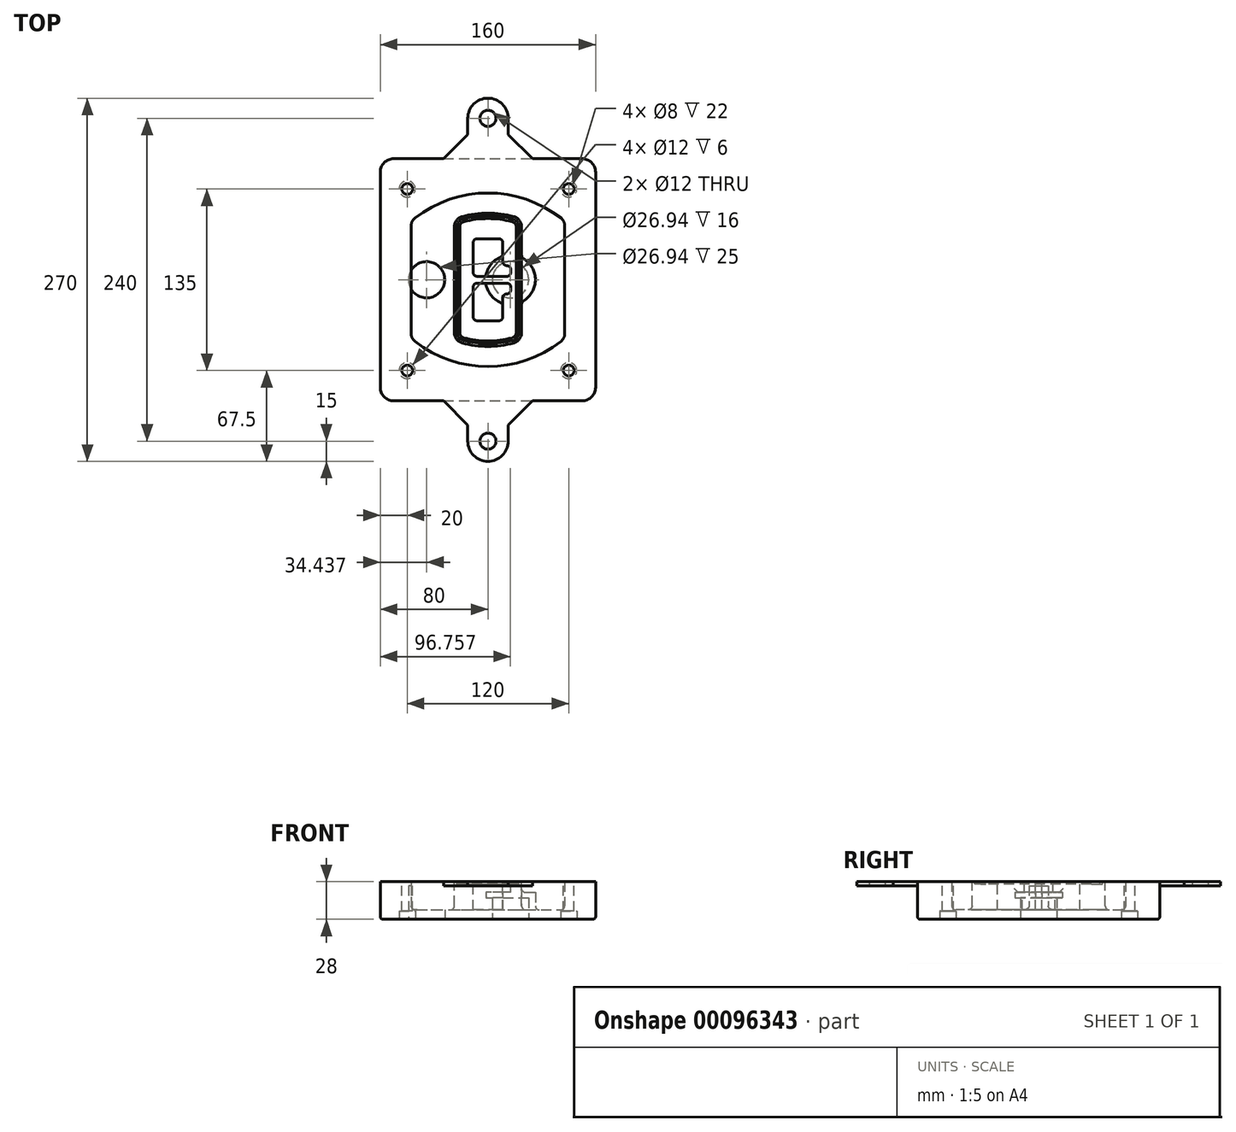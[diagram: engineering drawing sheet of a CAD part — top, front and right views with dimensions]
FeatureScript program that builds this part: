
annotation { "Feature Type Name" : "Feature", "Feature Type Description" : "" }
export const myFeature = defineFeature(function(context is Context, id is Id, definition is map)
    precondition{}
    {
        {
            var Q0;
            Q0=qCreatedBy(makeId("Top.planeOp"),FACE);
            var sketch = newSketch(context, id + "F0", { "sketchPlane" : qUnion([Q0])});
            skPoint(sketch, "E0.rect.middle", {"position": v(0, 0) * mm});
            skLineSegment(sketch, "E1.bottom", {"start": v(-70, -90) * mm, "end": v(70, -90) * mm});
            skLineSegment(sketch, "E1.top", {"start": v(-70, 90) * mm, "end": v(70, 90) * mm});
            skLineSegment(sketch, "E1.left", {"start": v(-80, -80) * mm, "end": v(-80, 80) * mm});
            skLineSegment(sketch, "E1.right", {"start": v(80, -80) * mm, "end": v(80, 80) * mm});
            skLineSegment(sketch, "E2", {"start": v(-80, 90) * mm, "end": v(80, -90) * mm, "construction": true});
            skLineSegment(sketch, "E3", {"start": v(80, 90) * mm, "end": v(-80, -90) * mm, "construction": true});
            skCircle(sketch, "E4", {"center": v(-60, 67.5) * mm, "radius": 4 * mm});
            skCircle(sketch, "E5", {"center": v(60, 67.5) * mm, "radius": 4 * mm});
            skCircle(sketch, "E6", {"center": v(60, -67.5) * mm, "radius": 4 * mm});
            skCircle(sketch, "E7", {"center": v(-60, -67.5) * mm, "radius": 4 * mm});
            skLineSegment(sketch, "E8", {"start": v(-60, 67.5) * mm, "end": v(60, 67.5) * mm, "construction": true});
            skLineSegment(sketch, "E9", {"start": v(60, 67.5) * mm, "end": v(60, -67.5) * mm, "construction": true});
            skLineSegment(sketch, "E10", {"start": v(60, -67.5) * mm, "end": v(-60, -67.5) * mm, "construction": true});
            skLineSegment(sketch, "E11", {"start": v(-60, -67.5) * mm, "end": v(-60, 67.5) * mm, "construction": true});
            skLineSegment(sketch, "E12", {"start": v(-60, 40.3) * mm, "end": v(-60, -40.3) * mm});
            skLineSegment(sketch, "E13", {"start": v(60, 40.3) * mm, "end": v(60, -40.3) * mm});
            skArc(sketch, "E14", {"start": v(56.15, 48.18) * mm, "mid": v(0, 67.5) * mm, "end": v(-56.15, 48.18) * mm});
            skArc(sketch, "E15", {"start": v(-56.15, -48.18) * mm, "mid": v(0, -67.5) * mm, "end": v(56.15, -48.18) * mm});
            skLineSegment(sketch, "E16", {"start": v(-60, 0) * mm, "end": v(60, 0) * mm, "construction": true});
            skPoint(sketch, "E17.visualSharp", {"position": v(-60, -45) * mm});
            skArc(sketch, "E17.filletArc", {"start": v(-60, -40.3) * mm, "mid": v(-58.99, -44.68) * mm, "end": v(-56.15, -48.18) * mm});
            skPoint(sketch, "E18.visualSharp", {"position": v(-60, 45) * mm});
            skArc(sketch, "E18.filletArc", {"start": v(-56.15, 48.18) * mm, "mid": v(-58.99, 44.68) * mm, "end": v(-60, 40.3) * mm});
            skPoint(sketch, "E19.visualSharp", {"position": v(60, 45) * mm});
            skArc(sketch, "E19.filletArc", {"start": v(60, 40.3) * mm, "mid": v(58.99, 44.68) * mm, "end": v(56.15, 48.18) * mm});
            skPoint(sketch, "E20.visualSharp", {"position": v(60, -45) * mm});
            skArc(sketch, "E20.filletArc", {"start": v(56.15, -48.18) * mm, "mid": v(58.99, -44.68) * mm, "end": v(60, -40.3) * mm});
            skPoint(sketch, "E21.visualSharp", {"position": v(-80, 90) * mm});
            skArc(sketch, "E21.filletArc", {"start": v(-70, 90) * mm, "mid": v(-77.07, 87.07) * mm, "end": v(-80, 80) * mm});
            skPoint(sketch, "E22.visualSharp", {"position": v(80, 90) * mm});
            skArc(sketch, "E22.filletArc", {"start": v(80, 80) * mm, "mid": v(77.07, 87.07) * mm, "end": v(70, 90) * mm});
            skPoint(sketch, "E23.visualSharp", {"position": v(80, -90) * mm});
            skArc(sketch, "E23.filletArc", {"start": v(70, -90) * mm, "mid": v(77.07, -87.07) * mm, "end": v(80, -80) * mm});
            skPoint(sketch, "E24.visualSharp", {"position": v(-80, -90) * mm});
            skArc(sketch, "E24.filletArc", {"start": v(-80, -80) * mm, "mid": v(-77.07, -87.07) * mm, "end": v(-70, -90) * mm});
            skArc(sketch, "E25.0", {"start": v(57, 40.3) * mm, "mid": v(56.3, 43.36) * mm, "end": v(54.3, 45.81) * mm});
            skLineSegment(sketch, "E25.1", {"start": v(57, 40.3) * mm, "end": v(57, -40.3) * mm});
            skArc(sketch, "E25.2", {"start": v(54.3, -45.81) * mm, "mid": v(56.3, -43.36) * mm, "end": v(57, -40.3) * mm});
            skArc(sketch, "E25.3", {"start": v(-54.3, -45.81) * mm, "mid": v(0, -64.5) * mm, "end": v(54.3, -45.81) * mm});
            skArc(sketch, "E25.4", {"start": v(-57, -40.3) * mm, "mid": v(-56.3, -43.36) * mm, "end": v(-54.3, -45.81) * mm});
            skArc(sketch, "E25.5", {"start": v(54.3, 45.81) * mm, "mid": v(0, 64.5) * mm, "end": v(-54.3, 45.81) * mm});
            skLineSegment(sketch, "E25.6", {"start": v(-57, 40.3) * mm, "end": v(-57, -40.3) * mm});
            skArc(sketch, "E25.7", {"start": v(-54.3, 45.81) * mm, "mid": v(-56.3, 43.36) * mm, "end": v(-57, 40.3) * mm});
            skArc(sketch, "E26.0", {"start": v(-58.62, 51.33) * mm, "mid": v(-62.58, 46.43) * mm, "end": v(-64, 40.3) * mm});
            skArc(sketch, "E26.1", {"start": v(58.62, 51.33) * mm, "mid": v(0, 71.5) * mm, "end": v(-58.62, 51.33) * mm});
            skArc(sketch, "E26.2", {"start": v(64, 40.3) * mm, "mid": v(62.58, 46.43) * mm, "end": v(58.62, 51.33) * mm});
            skLineSegment(sketch, "E26.3", {"start": v(64, 40.3) * mm, "end": v(64, -40.3) * mm});
            skArc(sketch, "E26.4", {"start": v(58.62, -51.33) * mm, "mid": v(62.58, -46.43) * mm, "end": v(64, -40.3) * mm});
            skLineSegment(sketch, "E26.5", {"start": v(-64, 40.3) * mm, "end": v(-64, -40.3) * mm});
            skArc(sketch, "E26.6", {"start": v(-58.62, -51.33) * mm, "mid": v(0, -71.5) * mm, "end": v(58.62, -51.33) * mm});
            skArc(sketch, "E26.7", {"start": v(-64, -40.3) * mm, "mid": v(-62.58, -46.43) * mm, "end": v(-58.62, -51.33) * mm});
            skSolve(sketch);
        }
        {
            var Q0;
            Q0=makeQuery(id+"F0.imprint","IMPRINT",FACE,{"disambiguationData":[TD([[makeQuery(id+"F0.imprint","IMPRINT",EDGE,{"derivedFrom":sQuery(id+"F0.wireOp",EDGE,"E1.bottom")}),1.0]])]});
            var Q1;
            Q1=makeQuery(id+"F0.imprint","IMPRINT",FACE,{"disambiguationData":[TD([[makeQuery(id+"F0.imprint","IMPRINT",EDGE,{"derivedFrom":sQuery(id+"F0.wireOp",EDGE,"E12")}),1.0]])]});
            var Q2;
            Q2=makeQuery(id+"F0.imprint","IMPRINT",FACE,{"disambiguationData":[TD([[makeQuery(id+"F0.imprint","IMPRINT",EDGE,{"derivedFrom":sQuery(id+"F0.wireOp",EDGE,"E25.0")}),1.0]])]});
            var Q3;
            Q3=makeQuery(id+"F0.imprint","IMPRINT",FACE,{"disambiguationData":[TD([[makeQuery(id+"F0.imprint","IMPRINT",EDGE,{"derivedFrom":sQuery(id+"F0.wireOp",EDGE,"E12")}),-1.0]])]});
            extrude(context, id + "F1", {"entities" : qUnion([Q0, Q1, Q2, Q3]), "oppositeDirection" : true, "depth" : 25 * mm});
        }
        {
            var Q0;
            Q0=makeQuery(id+"F0.imprint","IMPRINT",FACE,{"disambiguationData":[TD([[makeQuery(id+"F0.imprint","IMPRINT",EDGE,{"derivedFrom":sQuery(id+"F0.wireOp",EDGE,"E12")}),1.0]])]});
            extrude(context, id + "F2", {"entities" : qUnion([Q0]), "operationType" : NewBodyOperationType.ADD, "depth" : 3 * mm});
        }
        {
            var Q0;
            Q0=makeQuery(id+"F0.imprint","IMPRINT",FACE,{"disambiguationData":[TD([[makeQuery(id+"F0.imprint","IMPRINT",EDGE,{"derivedFrom":sQuery(id+"F0.wireOp",EDGE,"E25.0")}),1.0]])]});
            extrude(context, id + "F3", {"entities" : qUnion([Q0]), "operationType" : NewBodyOperationType.REMOVE, "oppositeDirection" : true, "depth" : 18 * mm});
        }
        {
            var Q0;
            Q0=makeQuery(id+"F2.opExtrude","CAP_FACE",FACE,{"disambiguationData":[OSD([sQuery(id+"F0.wireOp",EDGE,"E12"),sQuery(id+"F0.wireOp",EDGE,"E13"),sQuery(id+"F0.wireOp",EDGE,"E14"),sQuery(id+"F0.wireOp",EDGE,"E15"),sQuery(id+"F0.wireOp",EDGE,"E17.filletArc"),sQuery(id+"F0.wireOp",EDGE,"E18.filletArc"),sQuery(id+"F0.wireOp",EDGE,"E19.filletArc"),sQuery(id+"F0.wireOp",EDGE,"E20.filletArc"),sQuery(id+"F0.wireOp",EDGE,"E25.0"),sQuery(id+"F0.wireOp",EDGE,"E25.1"),sQuery(id+"F0.wireOp",EDGE,"E25.2"),sQuery(id+"F0.wireOp",EDGE,"E25.3"),sQuery(id+"F0.wireOp",EDGE,"E25.4"),sQuery(id+"F0.wireOp",EDGE,"E25.5"),sQuery(id+"F0.wireOp",EDGE,"E25.6"),sQuery(id+"F0.wireOp",EDGE,"E25.7")])],"isStart":false});
            var sketch = newSketch(context, id + "F4", { "sketchPlane" : qUnion([Q0])});
            skArc(sketch, "E27.0", {"start": v(-19.08, -46.97) * mm, "mid": v(0, -49.5) * mm, "end": v(19.08, -46.97) * mm});
            skArc(sketch, "E28.0", {"start": v(19.08, 46.97) * mm, "mid": v(0, 49.5) * mm, "end": v(-19.08, 46.97) * mm});
            skLineSegment(sketch, "E29", {"start": v(-25, 39.25) * mm, "end": v(-25, -39.25) * mm});
            skLineSegment(sketch, "E30", {"start": v(25, 39.25) * mm, "end": v(25, -39.25) * mm});
            skLineSegment(sketch, "E31", {"start": v(-25, 45.1) * mm, "end": v(25, 45.1) * mm, "construction": true});
            skLineSegment(sketch, "E32", {"start": v(-25, -45.1) * mm, "end": v(25, -45.1) * mm, "construction": true});
            skPoint(sketch, "E33.visualSharp", {"position": v(-25, 45.1) * mm});
            skArc(sketch, "E33.filletArc", {"start": v(-19.08, 46.97) * mm, "mid": v(-23.35, 44.11) * mm, "end": v(-25, 39.25) * mm});
            skPoint(sketch, "E34.visualSharp", {"position": v(25, 45.1) * mm});
            skArc(sketch, "E34.filletArc", {"start": v(25, 39.25) * mm, "mid": v(23.35, 44.11) * mm, "end": v(19.08, 46.97) * mm});
            skPoint(sketch, "E35.visualSharp", {"position": v(25, -45.1) * mm});
            skArc(sketch, "E35.filletArc", {"start": v(19.08, -46.97) * mm, "mid": v(23.35, -44.11) * mm, "end": v(25, -39.25) * mm});
            skPoint(sketch, "E36.visualSharp", {"position": v(-25, -45.1) * mm});
            skArc(sketch, "E36.filletArc", {"start": v(-25, -39.25) * mm, "mid": v(-23.35, -44.11) * mm, "end": v(-19.08, -46.97) * mm});
            skArc(sketch, "E37.0", {"start": v(54.3, 45.81) * mm, "mid": v(0, 64.5) * mm, "end": v(-54.3, 45.81) * mm});
            skArc(sketch, "E37.1", {"start": v(-54.3, 45.81) * mm, "mid": v(-56.3, 43.36) * mm, "end": v(-57, 40.3) * mm});
            skLineSegment(sketch, "E37.2", {"start": v(-57, 40.3) * mm, "end": v(-57, -40.3) * mm});
            skArc(sketch, "E37.3", {"start": v(-57, -40.3) * mm, "mid": v(-56.3, -43.36) * mm, "end": v(-54.3, -45.81) * mm});
            skArc(sketch, "E37.4", {"start": v(-54.3, -45.81) * mm, "mid": v(0, -64.5) * mm, "end": v(54.3, -45.81) * mm});
            skArc(sketch, "E37.5", {"start": v(54.3, -45.81) * mm, "mid": v(56.3, -43.36) * mm, "end": v(57, -40.3) * mm});
            skLineSegment(sketch, "E37.6", {"start": v(57, 40.3) * mm, "end": v(57, -40.3) * mm});
            skArc(sketch, "E37.7", {"start": v(57, 40.3) * mm, "mid": v(56.3, 43.36) * mm, "end": v(54.3, 45.81) * mm});
            skLineSegment(sketch, "E38.0", {"start": v(23, 39.25) * mm, "end": v(23, -39.25) * mm});
            skArc(sketch, "E38.1", {"start": v(18.56, -45.04) * mm, "mid": v(21.76, -42.9) * mm, "end": v(23, -39.25) * mm});
            skArc(sketch, "E38.2", {"start": v(-18.56, -45.04) * mm, "mid": v(0, -47.5) * mm, "end": v(18.56, -45.04) * mm});
            skArc(sketch, "E38.3", {"start": v(-23, -39.25) * mm, "mid": v(-21.76, -42.9) * mm, "end": v(-18.56, -45.04) * mm});
            skLineSegment(sketch, "E38.4", {"start": v(-23, 39.25) * mm, "end": v(-23, -39.25) * mm});
            skArc(sketch, "E38.5", {"start": v(23, 39.25) * mm, "mid": v(21.76, 42.9) * mm, "end": v(18.56, 45.04) * mm});
            skArc(sketch, "E38.6", {"start": v(-18.56, 45.04) * mm, "mid": v(-21.76, 42.9) * mm, "end": v(-23, 39.25) * mm});
            skArc(sketch, "E38.7", {"start": v(18.56, 45.04) * mm, "mid": v(0, 47.5) * mm, "end": v(-18.56, 45.04) * mm});
            skArc(sketch, "E39.0", {"start": v(21, 39.25) * mm, "mid": v(20.18, 41.68) * mm, "end": v(18.04, 43.1) * mm});
            skLineSegment(sketch, "E39.1", {"start": v(21, 39.25) * mm, "end": v(21, -39.25) * mm});
            skArc(sketch, "E39.2", {"start": v(18.04, -43.1) * mm, "mid": v(20.18, -41.68) * mm, "end": v(21, -39.25) * mm});
            skArc(sketch, "E39.3", {"start": v(-18.04, -43.1) * mm, "mid": v(0, -45.5) * mm, "end": v(18.04, -43.1) * mm});
            skArc(sketch, "E39.4", {"start": v(-21, -39.25) * mm, "mid": v(-20.18, -41.68) * mm, "end": v(-18.04, -43.1) * mm});
            skArc(sketch, "E39.5", {"start": v(18.04, 43.1) * mm, "mid": v(0, 45.5) * mm, "end": v(-18.04, 43.1) * mm});
            skLineSegment(sketch, "E39.6", {"start": v(-21, 39.25) * mm, "end": v(-21, -39.25) * mm});
            skArc(sketch, "E39.7", {"start": v(-18.04, 43.1) * mm, "mid": v(-20.18, 41.68) * mm, "end": v(-21, 39.25) * mm});
            skLineSegment(sketch, "E40", {"start": v(-25, 0) * mm, "end": v(25, 0) * mm, "construction": true});
            skLineSegment(sketch, "E41", {"start": v(-11, 5.5) * mm, "end": v(-11, 27.5) * mm});
            skLineSegment(sketch, "E42", {"start": v(-8, 30.5) * mm, "end": v(8, 30.5) * mm});
            skLineSegment(sketch, "E43", {"start": v(11, 27.5) * mm, "end": v(11, 13.5) * mm});
            skLineSegment(sketch, "E44", {"start": v(14, 10.5) * mm, "end": v(14, 10.5) * mm});
            skLineSegment(sketch, "E45", {"start": v(17, 7.5) * mm, "end": v(17, 5.5) * mm});
            skLineSegment(sketch, "E46", {"start": v(14, 2.5) * mm, "end": v(-8, 2.5) * mm});
            skPoint(sketch, "E47.visualSharp", {"position": v(-11, 30.5) * mm});
            skArc(sketch, "E47.filletArc", {"start": v(-8, 30.5) * mm, "mid": v(-10.12, 29.62) * mm, "end": v(-11, 27.5) * mm});
            skPoint(sketch, "E48.visualSharp", {"position": v(11, 30.5) * mm});
            skArc(sketch, "E48.filletArc", {"start": v(11, 27.5) * mm, "mid": v(10.12, 29.62) * mm, "end": v(8, 30.5) * mm});
            skPoint(sketch, "E49.visualSharp", {"position": v(11, 10.5) * mm});
            skArc(sketch, "E49.filletArc", {"start": v(11, 13.5) * mm, "mid": v(11.88, 11.38) * mm, "end": v(14, 10.5) * mm});
            skPoint(sketch, "E50.visualSharp", {"position": v(17, 10.5) * mm});
            skArc(sketch, "E50.filletArc", {"start": v(17, 7.5) * mm, "mid": v(16.12, 9.62) * mm, "end": v(14, 10.5) * mm});
            skPoint(sketch, "E51.visualSharp", {"position": v(17, 2.5) * mm});
            skArc(sketch, "E51.filletArc", {"start": v(14, 2.5) * mm, "mid": v(16.12, 3.38) * mm, "end": v(17, 5.5) * mm});
            skPoint(sketch, "E52.visualSharp", {"position": v(-11, 2.5) * mm});
            skArc(sketch, "E52.filletArc", {"start": v(-11, 5.5) * mm, "mid": v(-10.12, 3.38) * mm, "end": v(-8, 2.5) * mm});
            skLineSegment(sketch, "E53.0.MirrorCS", {"start": v(14, -2.5) * mm, "end": v(-8, -2.5) * mm});
            skArc(sketch, "E54.0.MirrorCS", {"start": v(-11, -5.5) * mm, "mid": v(-10.12, -3.38) * mm, "end": v(-8, -2.5) * mm});
            skLineSegment(sketch, "E55.0.MirrorCS", {"start": v(-11, -5.5) * mm, "end": v(-11, -27.5) * mm});
            skArc(sketch, "E56.0.MirrorCS", {"start": v(-8, -30.5) * mm, "mid": v(-10.12, -29.62) * mm, "end": v(-11, -27.5) * mm});
            skLineSegment(sketch, "E57.0.MirrorCS", {"start": v(-8, -30.5) * mm, "end": v(8, -30.5) * mm});
            skArc(sketch, "E58.0.MirrorCS", {"start": v(11, -27.5) * mm, "mid": v(10.12, -29.62) * mm, "end": v(8, -30.5) * mm});
            skLineSegment(sketch, "E59.0.MirrorCS", {"start": v(11, -27.5) * mm, "end": v(11, -13.5) * mm});
            skArc(sketch, "E60.0.MirrorCS", {"start": v(11, -13.5) * mm, "mid": v(11.88, -11.38) * mm, "end": v(14, -10.5) * mm});
            skArc(sketch, "E61.0.MirrorCS", {"start": v(17, -7.5) * mm, "mid": v(16.12, -9.62) * mm, "end": v(14, -10.5) * mm});
            skLineSegment(sketch, "E62.0.MirrorCS", {"start": v(17, -7.5) * mm, "end": v(17, -5.5) * mm});
            skArc(sketch, "E63.0.MirrorCS", {"start": v(14, -2.5) * mm, "mid": v(16.12, -3.38) * mm, "end": v(17, -5.5) * mm});
            skSolve(sketch);
        }
        {
            var Q0;
            Q0=makeQuery(id+"F4.imprint","IMPRINT",FACE,{"disambiguationData":[TD([[makeQuery(id+"F4.imprint","IMPRINT",EDGE,{"derivedFrom":sQuery(id+"F4.wireOp",EDGE,"E27.0")}),1.0]])]});
            var Q1;
            Q1=makeQuery(id+"F4.imprint","IMPRINT",FACE,{"disambiguationData":[TD([[makeQuery(id+"F4.imprint","IMPRINT",EDGE,{"derivedFrom":sQuery(id+"F4.wireOp",EDGE,"E38.0")}),-1.0]])]});
            var Q2;
            Q2=makeQuery(id+"F4.imprint","IMPRINT",FACE,{"disambiguationData":[TD([[makeQuery(id+"F4.imprint","IMPRINT",EDGE,{"derivedFrom":sQuery(id+"F4.wireOp",EDGE,"E39.0")}),1.0]])]});
            extrude(context, id + "F5", {"entities" : qUnion([Q0, Q1, Q2]), "operationType" : NewBodyOperationType.ADD, "endBound" : BoundingType.UP_TO_NEXT, "oppositeDirection" : true, "depth" : 25 * mm});
        }
        {
            var Q0;
            Q0=makeQuery(id+"F4.imprint","IMPRINT",FACE,{"disambiguationData":[TD([[makeQuery(id+"F4.imprint","IMPRINT",EDGE,{"derivedFrom":sQuery(id+"F4.wireOp",EDGE,"E38.0")}),-1.0]])]});
            extrude(context, id + "F6", {"entities" : qUnion([Q0]), "operationType" : NewBodyOperationType.REMOVE, "oppositeDirection" : true, "depth" : 2 * mm});
        }
        {
            var Q0;
            Q0=makeQuery(id+"F1.opExtrude","CAP_FACE",FACE,{"disambiguationData":[OSD([sQuery(id+"F0.wireOp",EDGE,"E1.bottom"),sQuery(id+"F0.wireOp",EDGE,"E1.top"),sQuery(id+"F0.wireOp",EDGE,"E1.left"),sQuery(id+"F0.wireOp",EDGE,"E1.right"),sQuery(id+"F0.wireOp",EDGE,"E4"),sQuery(id+"F0.wireOp",EDGE,"E5"),sQuery(id+"F0.wireOp",EDGE,"E6"),sQuery(id+"F0.wireOp",EDGE,"E7"),sQuery(id+"F0.wireOp",EDGE,"E21.filletArc"),sQuery(id+"F0.wireOp",EDGE,"E22.filletArc"),sQuery(id+"F0.wireOp",EDGE,"E23.filletArc"),sQuery(id+"F0.wireOp",EDGE,"E24.filletArc")])],"isStart":false});
            var sketch = newSketch(context, id + "F7", { "sketchPlane" : qUnion([Q0])});
            skCircle(sketch, "E64", {"center": v(16.76, 0) * mm, "radius": 13.47 * mm});
            skCircle(sketch, "E65", {"center": v(-45.56, 0) * mm, "radius": 13.47 * mm});
            skLineSegment(sketch, "E66", {"start": v(80, 0) * mm, "end": v(-80, 0) * mm});
            skCircle(sketch, "E67", {"center": v(16.76, 0) * mm, "radius": 18.47 * mm});
            skCircle(sketch, "E68", {"center": v(60, -67.5) * mm, "radius": 6 * mm});
            skCircle(sketch, "E69", {"center": v(-60, -67.5) * mm, "radius": 6 * mm});
            skCircle(sketch, "E70", {"center": v(-60, 67.5) * mm, "radius": 6 * mm});
            skCircle(sketch, "E71", {"center": v(60, 67.5) * mm, "radius": 6 * mm});
            skSolve(sketch);
        }
        {
            var Q0;
            {var subQ1=sQuery(id+"F7.wireOp",EDGE,"E66");var subQ4=sQuery(id+"F7.wireOp",EDGE,"E64");var subQ6=makeQuery(id+"F7.imprint","INTERSECT",VERTEX,{"disambiguationData":[OD(0.0)],"derivedFrom":[subQ4,subQ1]});Q0=makeQuery(id+"F7.imprint","IMPRINT",FACE,{"disambiguationData":[TD([[makeQuery(id+"F7.imprint","IMPRINT",EDGE,{"disambiguationData":[TD([[subQ6,-1.0]])],"derivedFrom":subQ4}),-1.0]])]});}
            var Q1;
            {var subQ0=sQuery(id+"F7.wireOp",EDGE,"E66");var subQ1=sQuery(id+"F7.wireOp",EDGE,"E64");var subQ3=makeQuery(id+"F7.imprint","INTERSECT",VERTEX,{"disambiguationData":[OD(0.0)],"derivedFrom":[subQ1,subQ0]});Q1=makeQuery(id+"F7.imprint","IMPRINT",FACE,{"disambiguationData":[TD([[makeQuery(id+"F7.imprint","IMPRINT",EDGE,{"disambiguationData":[TD([[subQ3,-1.0]])],"derivedFrom":subQ1}),1.0]])]});}
            var Q2;
            {var subQ0=sQuery(id+"F7.wireOp",EDGE,"E66");var subQ1=sQuery(id+"F7.wireOp",EDGE,"E64");var subQ3=makeQuery(id+"F7.imprint","INTERSECT",VERTEX,{"disambiguationData":[OD(0.0)],"derivedFrom":[subQ1,subQ0]});Q2=makeQuery(id+"F7.imprint","IMPRINT",FACE,{"disambiguationData":[TD([[makeQuery(id+"F7.imprint","IMPRINT",EDGE,{"disambiguationData":[TD([[subQ3,1.0]])],"derivedFrom":subQ1}),1.0]])]});}
            var Q3;
            {var subQ1=sQuery(id+"F7.wireOp",EDGE,"E66");var subQ4=sQuery(id+"F7.wireOp",EDGE,"E64");var subQ6=makeQuery(id+"F7.imprint","INTERSECT",VERTEX,{"disambiguationData":[OD(0.0)],"derivedFrom":[subQ4,subQ1]});Q3=makeQuery(id+"F7.imprint","IMPRINT",FACE,{"disambiguationData":[TD([[makeQuery(id+"F7.imprint","IMPRINT",EDGE,{"disambiguationData":[TD([[subQ6,1.0]])],"derivedFrom":subQ4}),-1.0]])]});}
            extrude(context, id + "F8", {"entities" : qUnion([Q0, Q1, Q2, Q3]), "operationType" : NewBodyOperationType.ADD, "oppositeDirection" : true, "depth" : 20 * mm});
        }
        {
            var Q0;
            {var subQ0=sQuery(id+"F7.wireOp",EDGE,"E66");var subQ1=sQuery(id+"F7.wireOp",EDGE,"E64");var subQ3=makeQuery(id+"F7.imprint","INTERSECT",VERTEX,{"disambiguationData":[OD(0.0)],"derivedFrom":[subQ1,subQ0]});Q0=makeQuery(id+"F7.imprint","IMPRINT",FACE,{"disambiguationData":[TD([[makeQuery(id+"F7.imprint","IMPRINT",EDGE,{"disambiguationData":[TD([[subQ3,-1.0]])],"derivedFrom":subQ1}),1.0]])]});}
            var Q1;
            {var subQ0=sQuery(id+"F7.wireOp",EDGE,"E66");var subQ1=sQuery(id+"F7.wireOp",EDGE,"E64");var subQ3=makeQuery(id+"F7.imprint","INTERSECT",VERTEX,{"disambiguationData":[OD(0.0)],"derivedFrom":[subQ1,subQ0]});Q1=makeQuery(id+"F7.imprint","IMPRINT",FACE,{"disambiguationData":[TD([[makeQuery(id+"F7.imprint","IMPRINT",EDGE,{"disambiguationData":[TD([[subQ3,1.0]])],"derivedFrom":subQ1}),1.0]])]});}
            extrude(context, id + "F9", {"entities" : qUnion([Q0, Q1]), "operationType" : NewBodyOperationType.REMOVE, "oppositeDirection" : true, "depth" : 16 * mm});
        }
        {
            var Q0;
            {var subQ0=sQuery(id+"F7.wireOp",EDGE,"E66");var subQ1=sQuery(id+"F7.wireOp",EDGE,"E65");var subQ3=makeQuery(id+"F7.imprint","INTERSECT",VERTEX,{"disambiguationData":[OD(0.0)],"derivedFrom":[subQ1,subQ0]});Q0=makeQuery(id+"F7.imprint","IMPRINT",FACE,{"disambiguationData":[TD([[makeQuery(id+"F7.imprint","IMPRINT",EDGE,{"disambiguationData":[TD([[subQ3,-1.0]])],"derivedFrom":subQ1}),1.0]])]});}
            var Q1;
            {var subQ0=sQuery(id+"F7.wireOp",EDGE,"E66");var subQ1=sQuery(id+"F7.wireOp",EDGE,"E65");var subQ3=makeQuery(id+"F7.imprint","INTERSECT",VERTEX,{"disambiguationData":[OD(0.0)],"derivedFrom":[subQ1,subQ0]});Q1=makeQuery(id+"F7.imprint","IMPRINT",FACE,{"disambiguationData":[TD([[makeQuery(id+"F7.imprint","IMPRINT",EDGE,{"disambiguationData":[TD([[subQ3,1.0]])],"derivedFrom":subQ1}),1.0]])]});}
            extrude(context, id + "F10", {"entities" : qUnion([Q0, Q1]), "operationType" : NewBodyOperationType.REMOVE, "oppositeDirection" : true, "depth" : 25 * mm});
        }
        {
            var Q0;
            Q0=makeQuery(id+"F7.imprint","IMPRINT",FACE,{"disambiguationData":[TD([[makeQuery(id+"F7.imprint","IMPRINT",EDGE,{"derivedFrom":sQuery(id+"F7.wireOp",EDGE,"E68")}),1.0]])]});
            var Q1;
            Q1=makeQuery(id+"F7.imprint","IMPRINT",FACE,{"disambiguationData":[TD([[makeQuery(id+"F7.imprint","IMPRINT",EDGE,{"derivedFrom":makeQuery(id+"F1.opExtrude","CAP_EDGE",EDGE,{"disambiguationData":[OSD([sQuery(id+"F0.wireOp",EDGE,"E5")])],"isStart":false})}),-1.0]])]});
            var Q2;
            Q2=makeQuery(id+"F7.imprint","IMPRINT",FACE,{"disambiguationData":[TD([[makeQuery(id+"F7.imprint","IMPRINT",EDGE,{"derivedFrom":sQuery(id+"F7.wireOp",EDGE,"E69")}),1.0]])]});
            var Q3;
            Q3=makeQuery(id+"F7.imprint","IMPRINT",FACE,{"disambiguationData":[TD([[makeQuery(id+"F7.imprint","IMPRINT",EDGE,{"derivedFrom":makeQuery(id+"F1.opExtrude","CAP_EDGE",EDGE,{"disambiguationData":[OSD([sQuery(id+"F0.wireOp",EDGE,"E4")])],"isStart":false})}),-1.0]])]});
            var Q4;
            Q4=makeQuery(id+"F7.imprint","IMPRINT",FACE,{"disambiguationData":[TD([[makeQuery(id+"F7.imprint","IMPRINT",EDGE,{"derivedFrom":sQuery(id+"F7.wireOp",EDGE,"E70")}),1.0]])]});
            var Q5;
            Q5=makeQuery(id+"F7.imprint","IMPRINT",FACE,{"disambiguationData":[TD([[makeQuery(id+"F7.imprint","IMPRINT",EDGE,{"derivedFrom":makeQuery(id+"F1.opExtrude","CAP_EDGE",EDGE,{"disambiguationData":[OSD([sQuery(id+"F0.wireOp",EDGE,"E7")])],"isStart":false})}),-1.0]])]});
            var Q6;
            Q6=makeQuery(id+"F7.imprint","IMPRINT",FACE,{"disambiguationData":[TD([[makeQuery(id+"F7.imprint","IMPRINT",EDGE,{"derivedFrom":sQuery(id+"F7.wireOp",EDGE,"E71")}),1.0]])]});
            var Q7;
            Q7=makeQuery(id+"F7.imprint","IMPRINT",FACE,{"disambiguationData":[TD([[makeQuery(id+"F7.imprint","IMPRINT",EDGE,{"derivedFrom":makeQuery(id+"F1.opExtrude","CAP_EDGE",EDGE,{"disambiguationData":[OSD([sQuery(id+"F0.wireOp",EDGE,"E6")])],"isStart":false})}),-1.0]])]});
            extrude(context, id + "F11", {"entities" : qUnion([Q0, Q1, Q2, Q3, Q4, Q5, Q6, Q7]), "operationType" : NewBodyOperationType.REMOVE, "oppositeDirection" : true, "depth" : 6 * mm});
        }
        {
            var Q0;
            Q0=makeQuery(id+"F9.boolean.opBoolean","COPY",FACE,{"derivedFrom":makeQuery(id+"F9.opExtrude","CAP_FACE",FACE,{"disambiguationData":[OSD([sQuery(id+"F7.wireOp",EDGE,"E64")])],"isStart":false})});
            var sketch = newSketch(context, id + "F12", { "sketchPlane" : qUnion([Q0])});
            skArc(sketch, "E72.0", {"start": v(11, 17.55) * mm, "mid": v(2.57, 11.82) * mm, "end": v(-1.54, 2.5) * mm});
            skArc(sketch, "E72.1", {"start": v(-1.54, -2.5) * mm, "mid": v(2.57, -11.82) * mm, "end": v(11, -17.55) * mm});
            skLineSegment(sketch, "E73", {"start": v(-1.54, -2.5) * mm, "end": v(14, -2.5) * mm});
            skLineSegment(sketch, "E74.0", {"start": v(14, 2.5) * mm, "end": v(-1.54, 2.5) * mm});
            skArc(sketch, "E74.1", {"start": v(14, 2.5) * mm, "mid": v(16.12, 3.38) * mm, "end": v(17, 5.5) * mm});
            skLineSegment(sketch, "E74.2", {"start": v(17, 7.5) * mm, "end": v(17, 5.5) * mm});
            skArc(sketch, "E74.3", {"start": v(17, 7.5) * mm, "mid": v(16.12, 9.62) * mm, "end": v(14, 10.5) * mm});
            skArc(sketch, "E74.4", {"start": v(11, 13.5) * mm, "mid": v(11.88, 11.38) * mm, "end": v(14, 10.5) * mm});
            skLineSegment(sketch, "E74.5", {"start": v(11, 17.55) * mm, "end": v(11, 13.5) * mm});
            skLineSegment(sketch, "E74.7", {"start": v(14, -2.5) * mm, "end": v(-1.54, -2.5) * mm});
            skArc(sketch, "E74.8", {"start": v(14, -2.5) * mm, "mid": v(16.12, -3.38) * mm, "end": v(17, -5.5) * mm});
            skLineSegment(sketch, "E74.9", {"start": v(17, -7.5) * mm, "end": v(17, -5.5) * mm});
            skArc(sketch, "E74.10", {"start": v(17, -7.5) * mm, "mid": v(16.12, -9.62) * mm, "end": v(14, -10.5) * mm});
            skArc(sketch, "E74.11", {"start": v(11, -13.5) * mm, "mid": v(11.88, -11.38) * mm, "end": v(14, -10.5) * mm});
            skLineSegment(sketch, "E74.12", {"start": v(11, -17.55) * mm, "end": v(11, -13.5) * mm});
            skPoint(sketch, "E75.orphan", {"position": v(11, -27.5) * mm});
            skPoint(sketch, "E76.orphan", {"position": v(-8, -2.5) * mm});
            skPoint(sketch, "E77.orphan", {"position": v(-8, 2.5) * mm});
            skPoint(sketch, "E78.orphan", {"position": v(11, 27.5) * mm});
            skSolve(sketch);
        }
        {
            var Q0;
            {var subQ7=sQuery(id+"F12.wireOp",EDGE,"E72.0");var subQ14=sQuery(id+"F12.wireOp",EDGE,"E72.1");var subQ16=sQuery(id+"F12.wireOp",EDGE,"E74.1");var subQ18=sQuery(id+"F12.wireOp",EDGE,"E74.8");Q0=qUnion([makeQuery(id+"F12.imprint","IMPRINT",FACE,{"disambiguationData":[TD([[makeQuery(id+"F12.imprint","IMPRINT",EDGE,{"derivedFrom":subQ7}),1.0]])]}),makeQuery(id+"F12.imprint","IMPRINT",FACE,{"disambiguationData":[TD([[makeQuery(id+"F12.imprint","IMPRINT",EDGE,{"derivedFrom":subQ14}),1.0]])]}),makeQuery(id+"F12.imprint","IMPRINT",FACE,{"disambiguationData":[TD([[makeQuery(id+"F12.imprint","IMPRINT",EDGE,{"derivedFrom":subQ16}),1.0]])]}),makeQuery(id+"F12.imprint","IMPRINT",FACE,{"disambiguationData":[TD([[makeQuery(id+"F12.imprint","IMPRINT",EDGE,{"derivedFrom":subQ18}),-1.0]])]})]);}
            var Q1;
            Q1=makeQuery(id+"F5.boolean.opBoolean","SPLIT",FACE,{"disambiguationData":[TD([makeQuery(id+"F5.opExtrude","SWEPT_FACE",FACE,{"disambiguationData":[OSD([sQuery(id+"F4.wireOp",EDGE,"E41")])]})])],"derivedFrom":makeQuery(id+"F3.boolean.opBoolean","COPY",FACE,{"derivedFrom":makeQuery(id+"F3.opExtrude","CAP_FACE",FACE,{"disambiguationData":[OSD([sQuery(id+"F0.wireOp",EDGE,"E25.0"),sQuery(id+"F0.wireOp",EDGE,"E25.1"),sQuery(id+"F0.wireOp",EDGE,"E25.2"),sQuery(id+"F0.wireOp",EDGE,"E25.3"),sQuery(id+"F0.wireOp",EDGE,"E25.4"),sQuery(id+"F0.wireOp",EDGE,"E25.5"),sQuery(id+"F0.wireOp",EDGE,"E25.6"),sQuery(id+"F0.wireOp",EDGE,"E25.7")])],"isStart":false})})});
            extrude(context, id + "F13", {"entities" : qUnion([Q0]), "operationType" : NewBodyOperationType.REMOVE, "endBound" : BoundingType.UP_TO_SURFACE, "endBoundEntityFace" : qUnion([Q1]), "depth" : 25 * mm});
        }
        {
            var Q0;
            Q0=makeQuery(id+"F3.boolean.opBoolean","COPY",EDGE,{"derivedFrom":makeQuery(id+"F3.opExtrude","CAP_EDGE",EDGE,{"disambiguationData":[OSD([sQuery(id+"F0.wireOp",EDGE,"E25.6")])],"isStart":false})});
            var Q1;
            Q1=makeQuery(id+"F8.boolean.opBoolean","INTERSECT",EDGE,{"derivedFrom":[makeQuery(id+"F5.opExtrude","SWEPT_FACE",FACE,{"disambiguationData":[OSD([sQuery(id+"F4.wireOp",EDGE,"E30")])]}),makeQuery(id+"F8.opExtrude","CAP_FACE",FACE,{"disambiguationData":[OSD([sQuery(id+"F7.wireOp",EDGE,"E67")])],"isStart":false})]});
            var Q2;
            Q2=makeQuery(id+"F8.boolean.opBoolean","INTERSECT",EDGE,{"disambiguationData":[OD(1.0)],"derivedFrom":[makeQuery(id+"F5.opExtrude","SWEPT_FACE",FACE,{"disambiguationData":[OSD([sQuery(id+"F4.wireOp",EDGE,"E30")])]}),makeQuery(id+"F8.opExtrude","SWEPT_FACE",FACE,{"disambiguationData":[OSD([sQuery(id+"F7.wireOp",EDGE,"E67")])]})]});
            var Q3;
            {var subQ0=sQuery(id+"F4.wireOp",EDGE,"E30");Q3=makeQuery(id+"F8.boolean.opBoolean","SPLIT",EDGE,{"disambiguationData":[TD([makeQuery(id+"F5.opExtrude","SWEPT_FACE",FACE,{"disambiguationData":[OSD([sQuery(id+"F4.wireOp",EDGE,"E35.filletArc")])]})])],"derivedFrom":makeQuery(id+"F5.opExtrude","CAP_EDGE",EDGE,{"disambiguationData":[OSD([subQ0])],"isStart":false})});}
            var Q4;
            {var subQ0=sQuery(id+"F0.wireOp",EDGE,"E25.7");var subQ1=sQuery(id+"F0.wireOp",EDGE,"E25.1");var subQ2=sQuery(id+"F0.wireOp",EDGE,"E25.6");var subQ3=sQuery(id+"F0.wireOp",EDGE,"E25.5");var subQ4=sQuery(id+"F0.wireOp",EDGE,"E25.4");var subQ5=sQuery(id+"F0.wireOp",EDGE,"E25.0");var subQ6=sQuery(id+"F0.wireOp",EDGE,"E25.2");var subQ7=sQuery(id+"F0.wireOp",EDGE,"E25.3");Q4=makeQuery(id+"F8.boolean.opBoolean","INTERSECT",EDGE,{"derivedFrom":[makeQuery(id+"F5.boolean.opBoolean","SPLIT",FACE,{"disambiguationData":[TD([makeQuery(id+"F2.opExtrude","SWEPT_FACE",FACE,{"disambiguationData":[OSD([subQ5])]})])],"derivedFrom":makeQuery(id+"F3.boolean.opBoolean","COPY",FACE,{"derivedFrom":makeQuery(id+"F3.opExtrude","CAP_FACE",FACE,{"disambiguationData":[OSD([subQ5,subQ1,subQ6,subQ7,subQ4,subQ3,subQ2,subQ0])],"isStart":false})})}),makeQuery(id+"F8.opExtrude","SWEPT_FACE",FACE,{"disambiguationData":[OSD([sQuery(id+"F7.wireOp",EDGE,"E67")])]})]});}
            var Q5;
            Q5=makeQuery(id+"F8.boolean.opBoolean","INTERSECT",EDGE,{"disambiguationData":[OD(0.0)],"derivedFrom":[makeQuery(id+"F5.opExtrude","SWEPT_FACE",FACE,{"disambiguationData":[OSD([sQuery(id+"F4.wireOp",EDGE,"E30")])]}),makeQuery(id+"F8.opExtrude","SWEPT_FACE",FACE,{"disambiguationData":[OSD([sQuery(id+"F7.wireOp",EDGE,"E67")])]})]});
            fillet(context, id + "F14", {"entities" : qUnion([Q0, Q1, Q2, Q3, Q4, Q5]), "radius" : 3 * mm, "tangentPropagation" : true, "allowEdgeOverflow" : false});
        }
        {
            var Q0;
            Q0=makeQuery(id+"F1.opExtrude","CAP_EDGE",EDGE,{"disambiguationData":[OSD([sQuery(id+"F0.wireOp",EDGE,"E1.bottom")])],"isStart":false});
            fillet(context, id + "F15", {"entities" : qUnion([Q0]), "radius" : 2 * mm, "tangentPropagation" : true, "allowEdgeOverflow" : false});
        }
        {
            var Q0;
            {var subQ0=sQuery(id+"F0.wireOp",EDGE,"E22.filletArc");var subQ1=sQuery(id+"F0.wireOp",EDGE,"E7");var subQ2=sQuery(id+"F0.wireOp",EDGE,"E6");var subQ3=sQuery(id+"F0.wireOp",EDGE,"E5");var subQ4=sQuery(id+"F0.wireOp",EDGE,"E4");var subQ5=sQuery(id+"F0.wireOp",EDGE,"E1.bottom");var subQ6=sQuery(id+"F0.wireOp",EDGE,"E21.filletArc");var subQ7=sQuery(id+"F0.wireOp",EDGE,"E1.top");var subQ8=sQuery(id+"F0.wireOp",EDGE,"E1.left");var subQ9=sQuery(id+"F0.wireOp",EDGE,"E1.right");var subQ10=sQuery(id+"F0.wireOp",EDGE,"E23.filletArc");var subQ11=sQuery(id+"F0.wireOp",EDGE,"E24.filletArc");Q0=makeQuery(id+"F2.boolean.opBoolean","SPLIT",FACE,{"disambiguationData":[TD([makeQuery(id+"F1.opExtrude","SWEPT_FACE",FACE,{"disambiguationData":[OSD([subQ5])]})])],"derivedFrom":makeQuery(id+"F1.opExtrude","CAP_FACE",FACE,{"disambiguationData":[OSD([subQ5,subQ7,subQ8,subQ9,subQ4,subQ3,subQ2,subQ1,subQ6,subQ0,subQ10,subQ11])],"isStart":true})});}
            var sketch = newSketch(context, id + "F16", { "sketchPlane" : qUnion([Q0])});
            skText(sketch, "E79", { "text": "The volume is 593914.627 mm3!\n", "fontName": "OpenSans-Regular.ttf"});
            const initialGuessF16  = {"E79": [-0.89864, -0.01858, 1, 0, 0.0393]};
            skSetInitialGuess(sketch, initialGuessF16);
            skSolve(sketch);
        }
        {
            var Q0;
            Q0=makeQuery(id+"F16.imprint","IMPRINT",FACE,{"disambiguationData":[TD([[makeQuery(id+"F16.imprint","IMPRINT",EDGE,{"derivedFrom":makeQuery(id+"F1.opExtrude","CAP_EDGE",EDGE,{"disambiguationData":[OSD([sQuery(id+"F0.wireOp",EDGE,"E1.bottom")])],"isStart":true})}),1.0]])]});
            var sketch = newSketch(context, id + "F17", { "sketchPlane" : qUnion([Q0])});
            skLineSegment(sketch, "E80", {"start": v(0, 90) * mm, "end": v(0, 120) * mm, "construction": true});
            skLineSegment(sketch, "E81", {"start": v(-15, 108) * mm, "end": v(-15, 120) * mm});
            skLineSegment(sketch, "E82", {"start": v(15, 108) * mm, "end": v(15, 120) * mm});
            skArc(sketch, "E83", {"start": v(15, 120) * mm, "mid": v(0, 135) * mm, "end": v(-15, 120) * mm});
            skLineSegment(sketch, "E84", {"start": v(-33, 90) * mm, "end": v(-15, 108) * mm});
            skLineSegment(sketch, "E85", {"start": v(15, 108) * mm, "end": v(33, 90) * mm});
            skCircle(sketch, "E86", {"center": v(0, 120) * mm, "radius": 6 * mm});
            skLineSegment(sketch, "E87", {"start": v(-75.2, 0) * mm, "end": v(74.09, 0) * mm, "construction": true});
            skLineSegment(sketch, "E88.MirrorCS", {"start": v(-33, -90) * mm, "end": v(-15, -108) * mm});
            skLineSegment(sketch, "E89.MirrorCS", {"start": v(-15, -108) * mm, "end": v(-15, -120) * mm});
            skArc(sketch, "E90.MirrorCS", {"start": v(15, -120) * mm, "mid": v(0, -135) * mm, "end": v(-15, -120) * mm});
            skLineSegment(sketch, "E91.MirrorCS", {"start": v(15, -108) * mm, "end": v(15, -120) * mm});
            skLineSegment(sketch, "E92.MirrorCS", {"start": v(15, -108) * mm, "end": v(33, -90) * mm});
            skCircle(sketch, "E93.MirrorC", {"center": v(0, -120) * mm, "radius": 6 * mm});
            skLineSegment(sketch, "E94.MirrorCS", {"start": v(0, -90) * mm, "end": v(0, -120) * mm, "construction": true});
            skSolve(sketch);
        }
        {
            var Q0;
            Q0=makeQuery(id+"F16.imprint","IMPRINT",FACE,{"disambiguationData":[TD([[makeQuery(id+"F16.imprint","IMPRINT",EDGE,{"derivedFrom":makeQuery(id+"F1.opExtrude","CAP_EDGE",EDGE,{"disambiguationData":[OSD([sQuery(id+"F0.wireOp",EDGE,"E1.bottom")])],"isStart":true})}),1.0]])]});
            var Q1;
            {var subQ0=sQuery(id+"F17.wireOp",EDGE,"E88.MirrorCS");Q1=makeQuery(id+"F17.imprint","IMPRINT",FACE,{"disambiguationData":[TD([[makeQuery(id+"F17.imprint","IMPRINT",EDGE,{"derivedFrom":subQ0}),1.0]])]});}
            var Q2;
            Q2=makeQuery(id+"F17.imprint","IMPRINT",FACE,{"disambiguationData":[TD([[makeQuery(id+"F17.imprint","IMPRINT",EDGE,{"derivedFrom":sQuery(id+"F17.wireOp",EDGE,"E81")}),-1.0]])]});
            var Q3;
            Q3=makeQuery(id+"F2.opExtrude","CAP_FACE",FACE,{"disambiguationData":[OSD([sQuery(id+"F0.wireOp",EDGE,"E12"),sQuery(id+"F0.wireOp",EDGE,"E13"),sQuery(id+"F0.wireOp",EDGE,"E14"),sQuery(id+"F0.wireOp",EDGE,"E15"),sQuery(id+"F0.wireOp",EDGE,"E17.filletArc"),sQuery(id+"F0.wireOp",EDGE,"E18.filletArc"),sQuery(id+"F0.wireOp",EDGE,"E19.filletArc"),sQuery(id+"F0.wireOp",EDGE,"E20.filletArc"),sQuery(id+"F0.wireOp",EDGE,"E25.0"),sQuery(id+"F0.wireOp",EDGE,"E25.1"),sQuery(id+"F0.wireOp",EDGE,"E25.2"),sQuery(id+"F0.wireOp",EDGE,"E25.3"),sQuery(id+"F0.wireOp",EDGE,"E25.4"),sQuery(id+"F0.wireOp",EDGE,"E25.5"),sQuery(id+"F0.wireOp",EDGE,"E25.6"),sQuery(id+"F0.wireOp",EDGE,"E25.7")])],"isStart":false});
            extrude(context, id + "F18", {"entities" : qUnion([Q0, Q1, Q2]), "operationType" : NewBodyOperationType.ADD, "endBound" : BoundingType.UP_TO_SURFACE, "endBoundEntityFace" : qUnion([Q3]), "depth" : 25 * mm});
        }
    });
